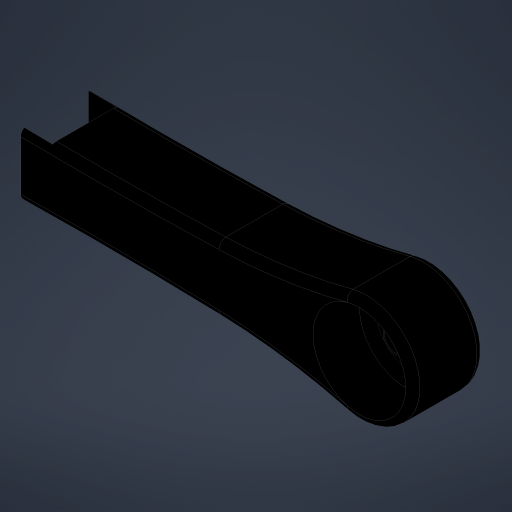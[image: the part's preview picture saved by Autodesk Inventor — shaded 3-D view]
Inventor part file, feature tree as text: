
AUTODESK INVENTOR PART (.ipt)
format: ipt  version: 2023 (Build 270158000, 158)  size: 296,448 bytes
history: native  units: mm
features: extrude x5, fillet x5, sketch x5, chamfer x1
ambient origin geometry x8: Origin, YZ Plane, XZ Plane, XY Plane, X Axis, Y Axis, Z Axis, Center Point
bodies: Solid1 (feature_tree)
feature tree (16):
  extrude  "Extrusion1"  Depth=50.0mm TaperAngle=0.0deg
  extrude  "Extrusion2"  Depth=40.0mm TaperAngle=0.0deg
  extrude  "Extrusion3"  Depth=17.0mm
  chamfer  "Chamfer1"  Distance=15.0mm
  fillet  "Fillet1"  Radius=10.0mm
  fillet  "Fillet2"  Radius=5.0mm
  fillet  "Fillet5"  Radius=200.0mm
  fillet  "Fillet6"  Radius=22.5mm
  extrude  "Extrusion5"  Depth=2.0mm
  extrude  "Extrusion6"  TaperAngle=135.0deg  [1 undecoded]
  fillet  "Fillet7"  Radius=400.0mm
  sketch  "Sketch1"  dims[d0=75.0mm d1=50.0mm d2=0.0mm]
  sketch  "Sketch2"  dims[d3=65.0mm d4=40.0mm d5=0.0mm]
  sketch  "Sketch3"  dims[d6=15.0mm d7=17.0mm d8=15.0mm d9=0.0mm]
  sketch  "Sketch5"  dims[d10=24.0mm d11=10.0mm d12=45.0deg d13=10.0mm d14=5.0mm d15=200.0mm d16=22.5mm]
  sketch  "Sketch6"  dims[d17=45.0mm d18=37.5mm d19=135.0deg d27=400.0mm d28=5.0mm d29=2.5mm d30=45.0mm d31=90.0deg d32=45.0mm d33=90.0deg d34=45.0mm d35=20.0mm d36=0.0mm d37=50.0mm d38=5.0mm d39=0.0mm d40=2.0mm d22=0.0mm d23=0.0mm d24=0.0mm d25=0.0mm]
note: 1 required parameter value undecoded (feature->parameter linkage not recoverable at this tier; creation-order binding heuristic only, values carry confidence <= 0.55)
